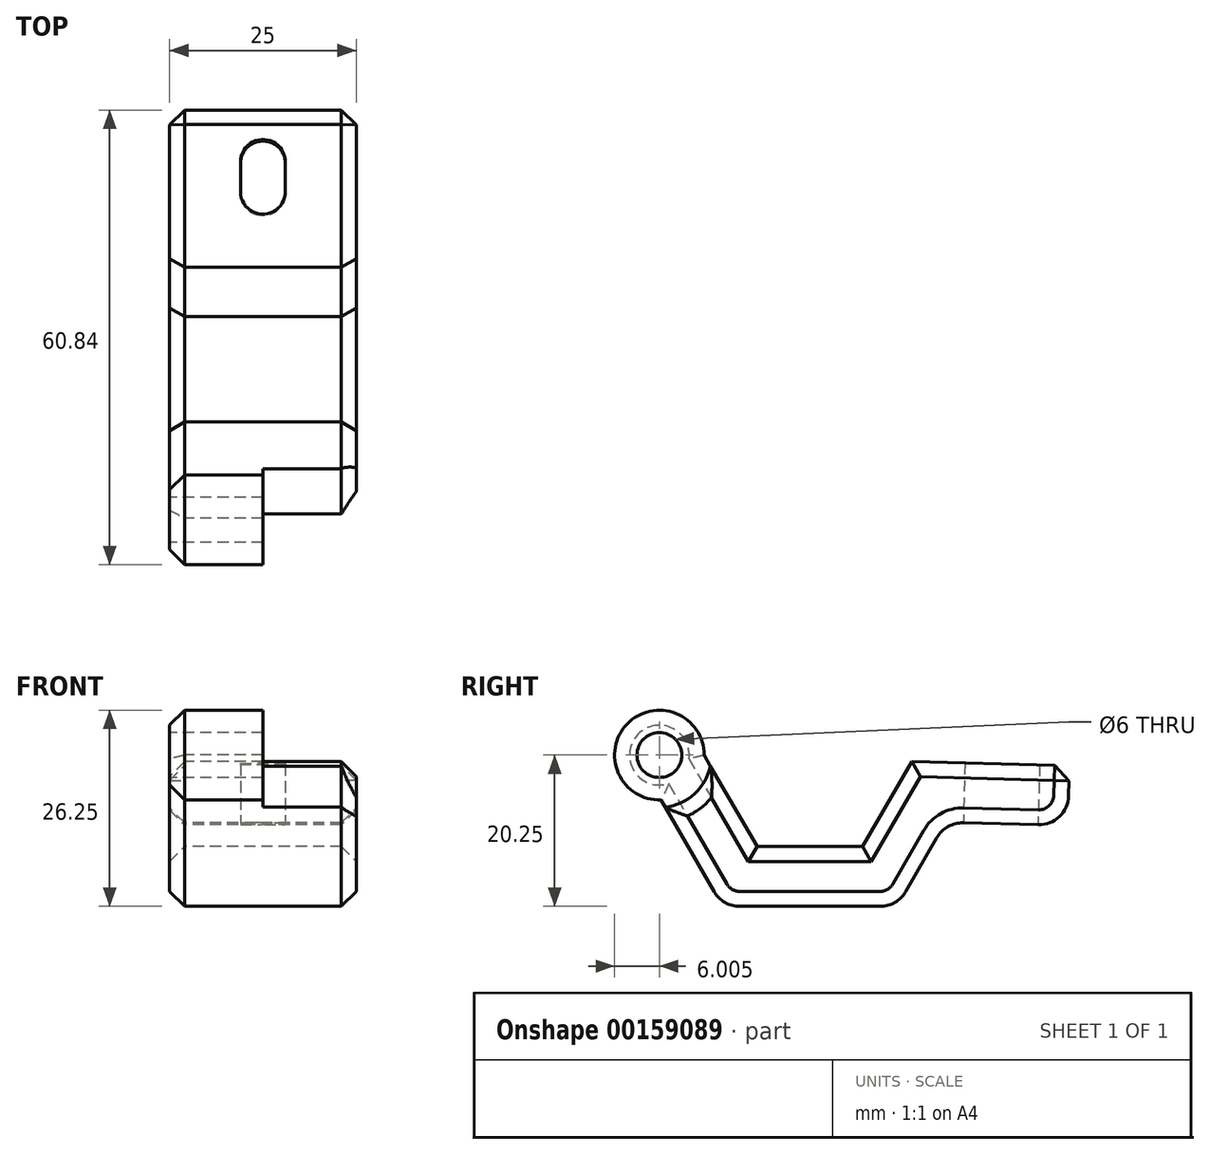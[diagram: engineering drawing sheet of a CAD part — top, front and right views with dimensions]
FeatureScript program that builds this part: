
annotation { "Feature Type Name" : "Feature", "Feature Type Description" : "" }
export const myFeature = defineFeature(function(context is Context, id is Id, definition is map)
    precondition{}
    {
        {
            var Q0;
            Q0=qCreatedBy(makeId("Right.planeOp"),FACE);
            var sketch = newSketch(context, id + "F0", { "sketchPlane" : qUnion([Q0])});
            skCircle(sketch, "E0.cCircle", {"center": v(0, 0) * mm, "radius": 12.25 * mm, "construction": true});
            skLineSegment(sketch, "E0.0", {"start": v(13.63, -0.88) * mm, "end": v(7.07, -12.25) * mm});
            skLineSegment(sketch, "E0.1", {"start": v(7.07, -12.25) * mm, "end": v(-7.07, -12.25) * mm});
            skLineSegment(sketch, "E0.2", {"start": v(-7.07, -12.25) * mm, "end": v(-14.15, 0) * mm});
            skLineSegment(sketch, "E1.2", {"start": v(17, -11.07) * mm, "end": v(12.85, -18.25) * mm});
            skLineSegment(sketch, "E1.4", {"start": v(9.38, -20.25) * mm, "end": v(-9.38, -20.25) * mm});
            skLineSegment(sketch, "E1.5", {"start": v(-12.85, -18.25) * mm, "end": v(-19.92, -6) * mm});
            skLineSegment(sketch, "E2.trimOffspring", {"start": v(-10.68, -6) * mm, "end": v(-10.68, -6) * mm});
            skLineSegment(sketch, "E3.trimOffspring", {"start": v(10.68, -6) * mm, "end": v(10.68, -6) * mm});
            skLineSegment(sketch, "E4.bottom", {"start": v(30.54, -9.33) * mm, "end": v(20.56, -9.07) * mm});
            skLineSegment(sketch, "E4.left", {"start": v(34.64, -5.44) * mm, "end": v(34.75, -1.44) * mm});
            skPoint(sketch, "E5.visualSharp", {"position": v(-11.7, -20.25) * mm});
            skArc(sketch, "E5.filletArc", {"start": v(-12.85, -18.25) * mm, "mid": v(-11.38, -19.71) * mm, "end": v(-9.38, -20.25) * mm});
            skPoint(sketch, "E6.visualSharp", {"position": v(11.7, -20.25) * mm});
            skArc(sketch, "E6.filletArc", {"start": v(9.38, -20.25) * mm, "mid": v(11.38, -19.71) * mm, "end": v(12.85, -18.25) * mm});
            skPoint(sketch, "E7.visualSharp", {"position": v(18.18, -9) * mm});
            skArc(sketch, "E7.filletArc", {"start": v(20.56, -9.07) * mm, "mid": v(18.5, -9.58) * mm, "end": v(17, -11.07) * mm});
            skPoint(sketch, "E8.visualSharp", {"position": v(34.54, -9.43) * mm});
            skArc(sketch, "E8.filletArc", {"start": v(30.54, -9.33) * mm, "mid": v(33.4, -8.23) * mm, "end": v(34.64, -5.44) * mm});
            skPoint(sketch, "E9", {"position": v(-39.04, 0) * mm});
            skCircle(sketch, "E10", {"center": v(-20.15, 0) * mm, "radius": 3 * mm});
            skCircle(sketch, "E11", {"center": v(-20.15, 0) * mm, "radius": 6 * mm});
            skLineSegment(sketch, "E12.trimOffspring", {"start": v(13.63, -0.88) * mm, "end": v(34.75, -1.44) * mm});
            skLineSegment(sketch, "E13", {"start": v(-20.15, 0) * mm, "end": v(34.75, -1.44) * mm, "construction": true});
            skSolve(sketch);
        }
        {
            var Q0;
            Q0 = qSketchRegion(id + "F0", true);
            extrude(context, id + "F1", {"entities" : qUnion([Q0]), "depth" : 25 * mm});
        }
        {
            var Q0;
            Q0=makeQuery(id+"F1.opExtrude","CAP_FACE",FACE,{"disambiguationData":[OSD([sQuery(id+"F0.wireOp",EDGE,"E0.0"),sQuery(id+"F0.wireOp",EDGE,"E0.1"),sQuery(id+"F0.wireOp",EDGE,"E0.2"),sQuery(id+"F0.wireOp",EDGE,"E1.2"),sQuery(id+"F0.wireOp",EDGE,"E1.4"),sQuery(id+"F0.wireOp",EDGE,"E1.5"),sQuery(id+"F0.wireOp",EDGE,"E4.bottom"),sQuery(id+"F0.wireOp",EDGE,"E4.left"),sQuery(id+"F0.wireOp",EDGE,"E5.filletArc"),sQuery(id+"F0.wireOp",EDGE,"E6.filletArc"),sQuery(id+"F0.wireOp",EDGE,"E7.filletArc"),sQuery(id+"F0.wireOp",EDGE,"E8.filletArc"),sQuery(id+"F0.wireOp",EDGE,"E10"),sQuery(id+"F0.wireOp",EDGE,"E11"),sQuery(id+"F0.wireOp",EDGE,"E12.trimOffspring")])],"isStart":false});
            var sketch = newSketch(context, id + "F2", { "sketchPlane" : qUnion([Q0])});
            skCircle(sketch, "E14", {"center": v(-20.15, 0) * mm, "radius": 7 * mm});
            skSolve(sketch);
        }
        {
            var Q0;
            Q0 = qSketchRegion(id + "F2", true);
            extrude(context, id + "F3", {"entities" : qUnion([Q0]), "operationType" : NewBodyOperationType.REMOVE, "oppositeDirection" : true, "depth" : 12.5 * mm});
        }
        {
            var Q0;
            Q0=makeQuery(id+"F1.opExtrude","SWEPT_FACE",FACE,{"disambiguationData":[OSD([sQuery(id+"F0.wireOp",EDGE,"E4.bottom")])]});
            var sketch = newSketch(context, id + "F4", { "sketchPlane" : qUnion([Q0])});
            skPoint(sketch, "E15.0.end.orphan", {"position": v(25, -20.8) * mm});
            skPoint(sketch, "E15.0.start.orphan", {"position": v(25, -30.77) * mm});
            skLineSegment(sketch, "E16", {"start": v(12.5, -23.78) * mm, "end": v(12.5, -27.78) * mm});
            skArc(sketch, "E17.0.startCap", {"start": v(9.5, -23.78) * mm, "mid": v(12.5, -20.78) * mm, "end": v(15.5, -23.78) * mm});
            skArc(sketch, "E17.0.endCap", {"start": v(15.5, -27.78) * mm, "mid": v(12.5, -30.78) * mm, "end": v(9.5, -27.78) * mm});
            skLineSegment(sketch, "E17.0.left", {"start": v(15.5, -23.78) * mm, "end": v(15.5, -27.78) * mm});
            skLineSegment(sketch, "E17.0.right", {"start": v(9.5, -23.78) * mm, "end": v(9.5, -27.78) * mm});
            skPoint(sketch, "E18", {"position": v(12.5, -25.78) * mm});
            skPoint(sketch, "E19", {"position": v(25, -25.78) * mm});
            skSolve(sketch);
        }
        {
            var Q0;
            Q0 = qSketchRegion(id + "F4", true);
            extrude(context, id + "F5", {"entities" : qUnion([Q0]), "operationType" : NewBodyOperationType.REMOVE, "oppositeDirection" : true, "depth" : 25 * mm});
        }
        {
            var Q0;
            Q0=makeQuery(id+"F1.opExtrude","CAP_FACE",FACE,{"disambiguationData":[OSD([sQuery(id+"F0.wireOp",EDGE,"E0.0"),sQuery(id+"F0.wireOp",EDGE,"E0.1"),sQuery(id+"F0.wireOp",EDGE,"E0.2"),sQuery(id+"F0.wireOp",EDGE,"E1.2"),sQuery(id+"F0.wireOp",EDGE,"E1.4"),sQuery(id+"F0.wireOp",EDGE,"E1.5"),sQuery(id+"F0.wireOp",EDGE,"E4.bottom"),sQuery(id+"F0.wireOp",EDGE,"E4.left"),sQuery(id+"F0.wireOp",EDGE,"E5.filletArc"),sQuery(id+"F0.wireOp",EDGE,"E6.filletArc"),sQuery(id+"F0.wireOp",EDGE,"E7.filletArc"),sQuery(id+"F0.wireOp",EDGE,"E8.filletArc"),sQuery(id+"F0.wireOp",EDGE,"E10"),sQuery(id+"F0.wireOp",EDGE,"E11"),sQuery(id+"F0.wireOp",EDGE,"E12.trimOffspring")])],"isStart":false});
            var Q1;
            Q1=makeQuery(id+"F1.opExtrude","CAP_EDGE",EDGE,{"disambiguationData":[OSD([sQuery(id+"F0.wireOp",EDGE,"E12.trimOffspring")])],"isStart":true});
            var Q2;
            Q2=makeQuery(id+"F1.opExtrude","CAP_EDGE",EDGE,{"disambiguationData":[OSD([sQuery(id+"F0.wireOp",EDGE,"E0.0")])],"isStart":true});
            var Q3;
            Q3=makeQuery(id+"F1.opExtrude","CAP_EDGE",EDGE,{"disambiguationData":[OSD([sQuery(id+"F0.wireOp",EDGE,"E0.1")])],"isStart":true});
            var Q4;
            Q4=makeQuery(id+"F1.opExtrude","CAP_EDGE",EDGE,{"disambiguationData":[OSD([sQuery(id+"F0.wireOp",EDGE,"E0.2")])],"isStart":true});
            var Q5;
            Q5=makeQuery(id+"F1.opExtrude","CAP_EDGE",EDGE,{"disambiguationData":[OSD([sQuery(id+"F0.wireOp",EDGE,"E11")])],"isStart":true});
            var Q6;
            Q6=makeQuery(id+"F1.opExtrude","CAP_EDGE",EDGE,{"disambiguationData":[OSD([sQuery(id+"F0.wireOp",EDGE,"E1.5")])],"isStart":true});
            var Q7;
            Q7=makeQuery(id+"F1.opExtrude","SWEPT_EDGE",EDGE,{"disambiguationData":[OSD([sQuery(id+"F0.wireOp",EDGE,"E4.left"),sQuery(id+"F0.wireOp",EDGE,"E12.trimOffspring")])]});
            chamfer(context, id + "F6", {"entities" : qUnion([Q0, Q1, Q2, Q3, Q4, Q5, Q6, Q7]), "width" : 2 * mm, "tangentPropagation" : true});
        }
    });
